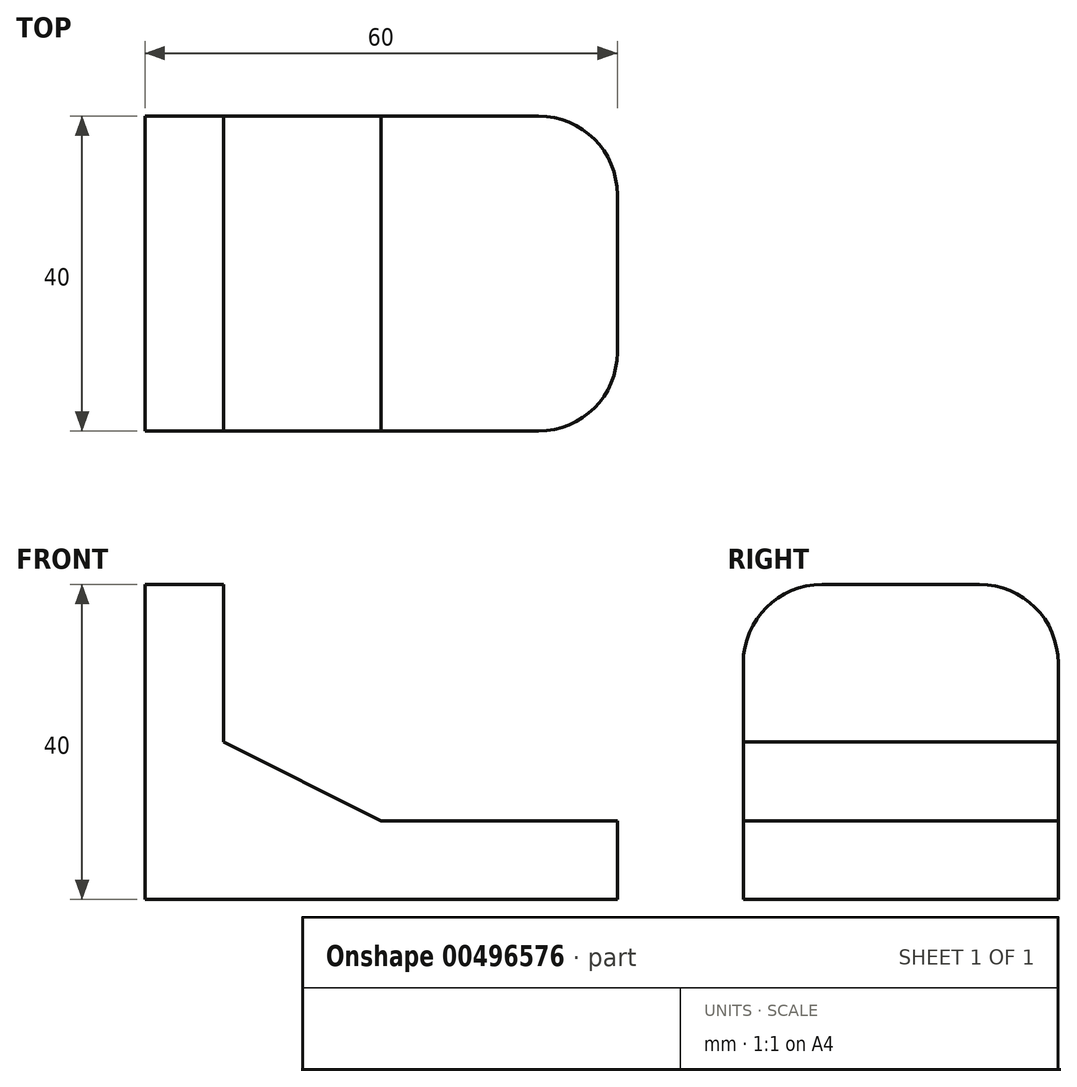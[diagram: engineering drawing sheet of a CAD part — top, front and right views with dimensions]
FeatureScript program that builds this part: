
annotation { "Feature Type Name" : "Feature", "Feature Type Description" : "" }
export const myFeature = defineFeature(function(context is Context, id is Id, definition is map)
    precondition{}
    {
        {
            var Q0;
            Q0=qCreatedBy(makeId("Front.planeOp"),FACE);
            var sketch = newSketch(context, id + "F0", { "sketchPlane" : qUnion([Q0])});
            skLineSegment(sketch, "E0", {"start": v(0, 0) * mm, "end": v(0, 40) * mm});
            skLineSegment(sketch, "E1", {"start": v(0, 40) * mm, "end": v(10, 40) * mm});
            skLineSegment(sketch, "E2", {"start": v(0, 0) * mm, "end": v(60, 0) * mm});
            skLineSegment(sketch, "E3", {"start": v(60, 0) * mm, "end": v(60, 10) * mm});
            skLineSegment(sketch, "E4", {"start": v(60, 10) * mm, "end": v(30, 10) * mm});
            skLineSegment(sketch, "E5", {"start": v(30, 10) * mm, "end": v(10, 20) * mm});
            skLineSegment(sketch, "E6", {"start": v(10, 40) * mm, "end": v(10, 20) * mm});
            skSolve(sketch);
        }
        {
            var Q0;
            Q0 = qSketchRegion(id + "F0", true);
            extrude(context, id + "F1", {"entities" : qUnion([Q0]), "depth" : 40 * mm});
        }
        {
            var Q0;
            Q0=makeQuery(id+"F1.opExtrude","CAP_EDGE",EDGE,{"disambiguationData":[OSD([sQuery(id+"F0.wireOp",EDGE,"E1")])],"isStart":false});
            var Q1;
            Q1=makeQuery(id+"F1.opExtrude","CAP_EDGE",EDGE,{"disambiguationData":[OSD([sQuery(id+"F0.wireOp",EDGE,"E1")])],"isStart":true});
            var Q2;
            Q2=makeQuery(id+"F1.opExtrude","CAP_EDGE",EDGE,{"disambiguationData":[OSD([sQuery(id+"F0.wireOp",EDGE,"E3")])],"isStart":true});
            var Q3;
            Q3=makeQuery(id+"F1.opExtrude","CAP_EDGE",EDGE,{"disambiguationData":[OSD([sQuery(id+"F0.wireOp",EDGE,"E3")])],"isStart":false});
            fillet(context, id + "F2", {"entities" : qUnion([Q0, Q1, Q2, Q3]), "radius" : 10 * mm, "tangentPropagation" : true, "allowEdgeOverflow" : false});
        }
    });
